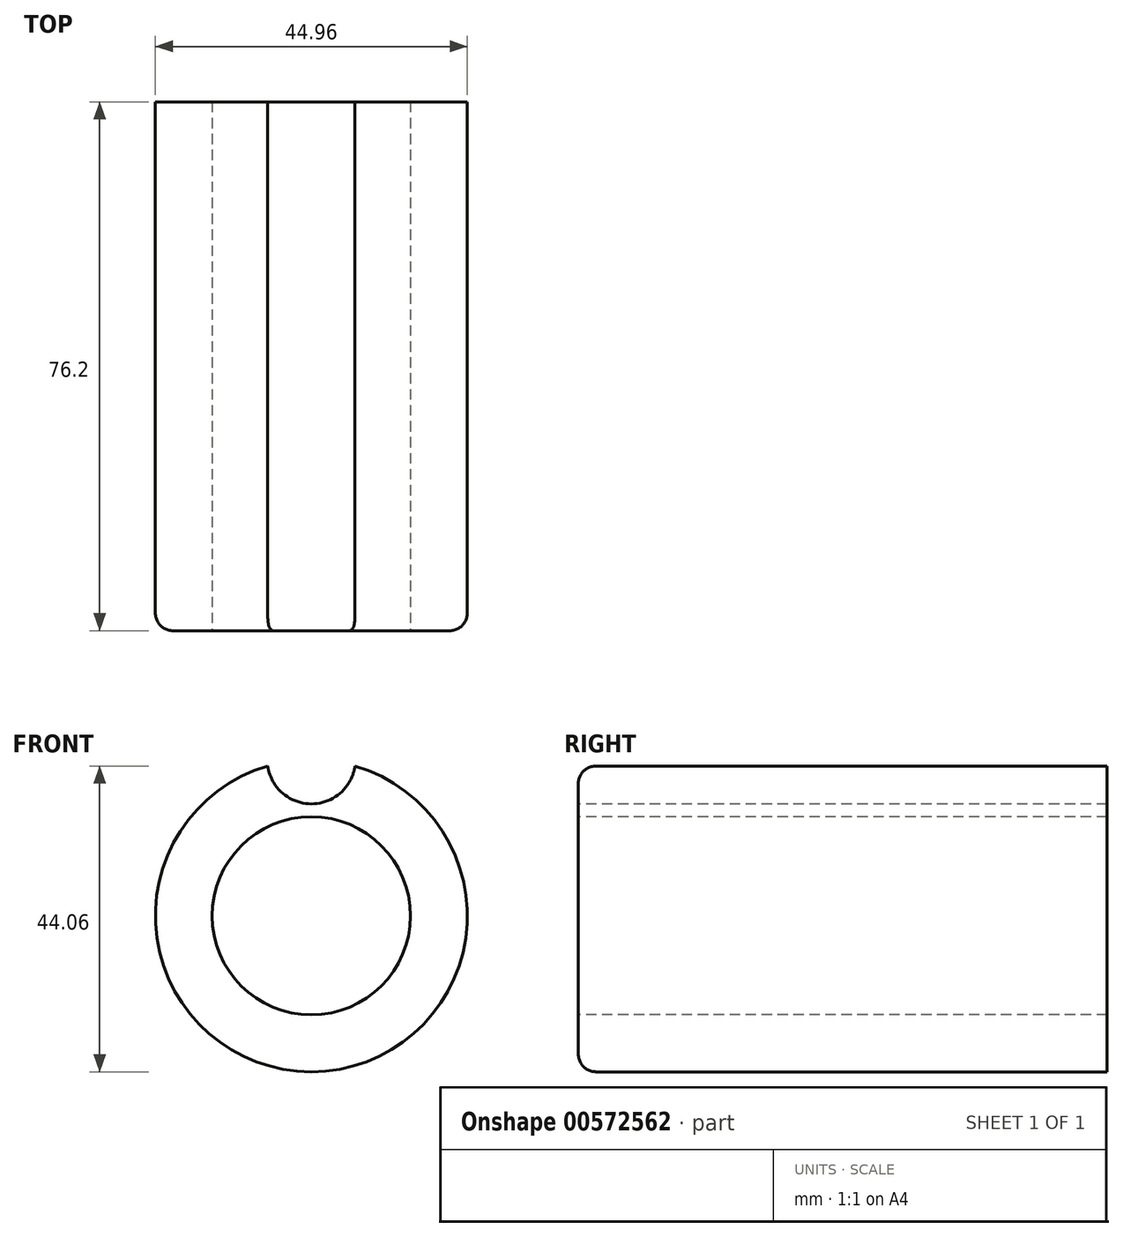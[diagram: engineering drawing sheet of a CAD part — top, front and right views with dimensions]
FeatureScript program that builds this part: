
annotation { "Feature Type Name" : "Feature", "Feature Type Description" : "" }
export const myFeature = defineFeature(function(context is Context, id is Id, definition is map)
    precondition{}
    {
        {
            var Q0;
            Q0=qCreatedBy(makeId("Front.planeOp"),FACE);
            var sketch = newSketch(context, id + "F0", { "sketchPlane" : qUnion([Q0])});
            skCircle(sketch, "E0", {"center": v(0, 0) * mm, "radius": 14.28 * mm});
            skCircle(sketch, "E1", {"center": v(0, 0) * mm, "radius": 22.48 * mm});
            skLineSegment(sketch, "E2", {"start": v(0, 22.48) * mm, "end": v(0, -49.68) * mm, "construction": true});
            skArc(sketch, "E3", {"start": v(-6.29, 21.58) * mm, "mid": v(0, 16.13) * mm, "end": v(6.29, 21.58) * mm});
            skPoint(sketch, "E4.orphan", {"position": v(0, 49.68) * mm});
            skSolve(sketch);
        }
        {
            var Q0;
            Q0=makeQuery(id+"F0.imprint","IMPRINT",FACE,{"disambiguationData":[TD([[makeQuery(id+"F0.imprint","IMPRINT",EDGE,{"derivedFrom":sQuery(id+"F0.wireOp",EDGE,"E0")}),-1.0]])]});
            extrude(context, id + "F1", {"entities" : qUnion([Q0]), "oppositeDirection" : true, "depth" : 25.4 * mm, "offsetDistance" : 25.4 * mm});
        }
        {
            var Q0;
            Q0=makeQuery(id+"F1.opExtrude","CAP_FACE",FACE,{"disambiguationData":[OSD([sQuery(id+"F0.wireOp",EDGE,"E0"),sQuery(id+"F0.wireOp",EDGE,"E1")])],"isStart":false});
            var Q1;
            Q1=makeQuery(id+"F1.opExtrude","CAP_FACE",FACE,{"disambiguationData":[OSD([sQuery(id+"F0.wireOp",EDGE,"E0"),sQuery(id+"F0.wireOp",EDGE,"E1")])],"isStart":true});
            extrude(context, id + "F2", {"entities" : qUnion([Q0, Q1]), "operationType" : NewBodyOperationType.ADD, "oppositeDirection" : true, "depth" : 50.8 * mm, "offsetDistance" : 25.4 * mm});
        }
        {
            var Q0;
            {var subQ0=sQuery(id+"F0.wireOp",EDGE,"E1");Q0=makeQuery(id+"F2.opExtrude","CAP_EDGE",EDGE,{"disambiguationData":[OSD([subQ0]),TDD([makeQuery(id+"F1.opExtrude","CAP_EDGE",EDGE,{"disambiguationData":[OSD([subQ0])],"isStart":true})])],"isStart":false});}
            fillet(context, id + "F3", {"entities" : qUnion([Q0]), "radius" : 2.54 * mm, "tangentPropagation" : true, "allowEdgeOverflow" : false});
        }
        {
            var Q0;
            {var subQ0=sQuery(id+"F0.wireOp",EDGE,"E3");Q0=makeQuery(id+"F0.imprint","IMPRINT",FACE,{"disambiguationData":[TD([[makeQuery(id+"F0.imprint","IMPRINT",EDGE,{"derivedFrom":subQ0}),1.0]])]});}
            extrude(context, id + "F4", {"entities" : qUnion([Q0]), "operationType" : NewBodyOperationType.REMOVE, "depth" : 76.2 * mm, "offsetDistance" : 25.4 * mm});
        }
    });
